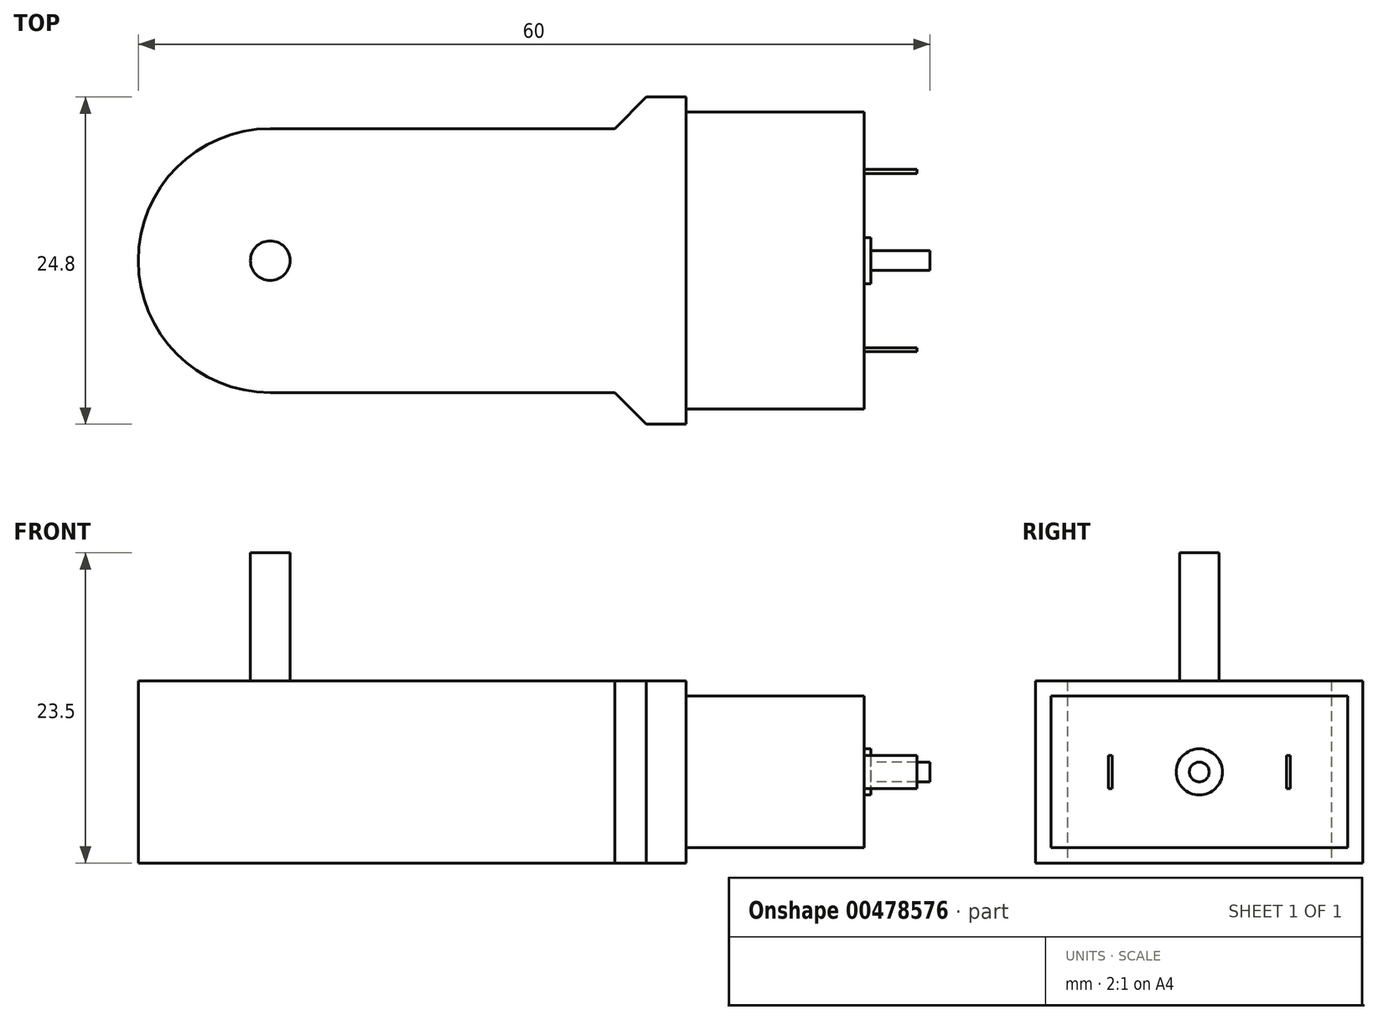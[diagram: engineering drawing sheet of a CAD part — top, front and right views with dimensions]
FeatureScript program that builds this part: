
annotation { "Feature Type Name" : "Feature", "Feature Type Description" : "" }
export const myFeature = defineFeature(function(context is Context, id is Id, definition is map)
    precondition{}
    {
        {
            var Q0;
            Q0=qCreatedBy(makeId("Top.planeOp"),FACE);
            var sketch = newSketch(context, id + "F0", { "sketchPlane" : qUnion([Q0])});
            skCircle(sketch, "E0", {"center": v(0, 0) * mm, "radius": 10 * mm});
            skLineSegment(sketch, "E1", {"start": v(0, 10) * mm, "end": v(26.1, 10) * mm});
            skLineSegment(sketch, "E2", {"start": v(26.1, 10) * mm, "end": v(28.5, 12.4) * mm});
            skLineSegment(sketch, "E3", {"start": v(28.5, 12.4) * mm, "end": v(31.5, 12.4) * mm});
            skLineSegment(sketch, "E4", {"start": v(31.5, 12.4) * mm, "end": v(31.5, 0) * mm});
            skLineSegment(sketch, "E5", {"start": v(0, 0) * mm, "end": v(31.5, 0) * mm, "construction": true});
            skLineSegment(sketch, "E6.MirrorCS", {"start": v(31.5, -12.4) * mm, "end": v(31.5, 0) * mm});
            skLineSegment(sketch, "E7.MirrorCS", {"start": v(28.5, -12.4) * mm, "end": v(31.5, -12.4) * mm});
            skLineSegment(sketch, "E8.MirrorCS", {"start": v(26.1, -10) * mm, "end": v(28.5, -12.4) * mm});
            skLineSegment(sketch, "E9.MirrorCS", {"start": v(0, -10) * mm, "end": v(26.1, -10) * mm});
            skSolve(sketch);
        }
        {
            var Q0;
            Q0 = qSketchRegion(id + "F0", true);
            extrude(context, id + "F1", {"entities" : qUnion([Q0]), "endBound" : BoundingType.SYMMETRIC, "depth" : 13.8 * mm});
        }
        {
            var Q0;
            Q0=qCreatedBy(makeId("Top.planeOp"),FACE);
            var sketch = newSketch(context, id + "F2", { "sketchPlane" : qUnion([Q0])});
            skCircle(sketch, "E10", {"center": v(0, 0) * mm, "radius": 1.5 * mm});
            skSolve(sketch);
        }
        {
            var Q0;
            Q0 = qSketchRegion(id + "F2", true);
            extrude(context, id + "F3", {"entities" : qUnion([Q0]), "operationType" : NewBodyOperationType.ADD, "depth" : 16.6 * mm});
        }
        {
            var Q0;
            Q0=qCreatedBy(makeId("Top.planeOp"),FACE);
            var sketch = newSketch(context, id + "F4", { "sketchPlane" : qUnion([Q0])});
            skPoint(sketch, "E11.0", {"position": v(31.5, 12.4) * mm});
            skPoint(sketch, "E12.0", {"position": v(31.5, -12.4) * mm});
            skLineSegment(sketch, "E13.bottom", {"start": v(31.5, -11.25) * mm, "end": v(45, -11.25) * mm});
            skLineSegment(sketch, "E13.top", {"start": v(31.5, 11.25) * mm, "end": v(45, 11.25) * mm});
            skLineSegment(sketch, "E13.left", {"start": v(31.5, -11.25) * mm, "end": v(31.5, 11.25) * mm});
            skLineSegment(sketch, "E13.right", {"start": v(45, -11.25) * mm, "end": v(45, 11.25) * mm});
            skLineSegment(sketch, "E14", {"start": v(31.5, 12.4) * mm, "end": v(31.5, 11.25) * mm, "construction": true});
            skLineSegment(sketch, "E15", {"start": v(0, 0) * mm, "end": v(31.5, 0) * mm, "construction": true});
            skSolve(sketch);
        }
        {
            var Q0;
            Q0=makeQuery(id+"F4.imprint","IMPRINT",FACE,{"disambiguationData":[TD([[makeQuery(id+"F4.imprint","IMPRINT",EDGE,{"derivedFrom":sQuery(id+"F4.wireOp",EDGE,"E13.bottom")}),1.0]])]});
            extrude(context, id + "F5", {"entities" : qUnion([Q0]), "operationType" : NewBodyOperationType.ADD, "endBound" : BoundingType.SYMMETRIC, "depth" : 11.5 * mm});
        }
        {
            var Q0;
            Q0=makeQuery(id+"F5.opExtrude","SWEPT_FACE",FACE,{"disambiguationData":[OSD([sQuery(id+"F4.wireOp",EDGE,"E13.right")])]});
            var sketch = newSketch(context, id + "F6", { "sketchPlane" : qUnion([Q0])});
            skLineSegment(sketch, "E16", {"start": v(-11.25, 0) * mm, "end": v(11.25, 0) * mm, "construction": true});
            skLineSegment(sketch, "E17", {"start": v(0, 5.75) * mm, "end": v(0, -5.75) * mm, "construction": true});
            skCircle(sketch, "E18", {"center": v(0, 0) * mm, "radius": 1.75 * mm});
            skSolve(sketch);
        }
        {
            var Q0;
            Q0 = qSketchRegion(id + "F6", true);
            extrude(context, id + "F7", {"entities" : qUnion([Q0]), "operationType" : NewBodyOperationType.ADD, "depth" : .5 * mm});
        }
        {
            var Q0;
            Q0=makeQuery(id+"F7.opExtrude","CAP_FACE",FACE,{"disambiguationData":[OSD([sQuery(id+"F6.wireOp",EDGE,"E18")])],"isStart":false});
            var sketch = newSketch(context, id + "F8", { "sketchPlane" : qUnion([Q0])});
            skCircle(sketch, "E19", {"center": v(0, 0) * mm, "radius": 0.75 * mm});
            skSolve(sketch);
        }
        {
            var Q0;
            Q0 = qSketchRegion(id + "F8", true);
            extrude(context, id + "F9", {"entities" : qUnion([Q0]), "operationType" : NewBodyOperationType.ADD, "depth" : 4.5 * mm});
        }
        {
            var Q0;
            Q0=makeQuery(id+"F5.opExtrude","SWEPT_FACE",FACE,{"disambiguationData":[OSD([sQuery(id+"F4.wireOp",EDGE,"E13.right")])]});
            var sketch = newSketch(context, id + "F10", { "sketchPlane" : qUnion([Q0])});
            skLineSegment(sketch, "E20", {"start": v(0, 5.75) * mm, "end": v(0, -5.75) * mm, "construction": true});
            skLineSegment(sketch, "E21.bottom", {"start": v(-6.9, 1.25) * mm, "end": v(-6.6, 1.25) * mm});
            skLineSegment(sketch, "E21.top", {"start": v(-6.9, -1.25) * mm, "end": v(-6.6, -1.25) * mm});
            skLineSegment(sketch, "E21.left", {"start": v(-6.9, 1.25) * mm, "end": v(-6.9, -1.25) * mm});
            skLineSegment(sketch, "E21.right", {"start": v(-6.6, 1.25) * mm, "end": v(-6.6, -1.25) * mm});
            skLineSegment(sketch, "E22", {"start": v(-6.6, 0) * mm, "end": v(0, 0) * mm, "construction": true});
            skLineSegment(sketch, "E23.MirrorCS", {"start": v(6.9, 1.25) * mm, "end": v(6.6, 1.25) * mm});
            skLineSegment(sketch, "E24.MirrorCS", {"start": v(6.9, -1.25) * mm, "end": v(6.6, -1.25) * mm});
            skLineSegment(sketch, "E25.MirrorCS", {"start": v(6.6, 1.25) * mm, "end": v(6.6, -1.25) * mm});
            skLineSegment(sketch, "E26.MirrorCS", {"start": v(6.9, 1.25) * mm, "end": v(6.9, -1.25) * mm});
            skLineSegment(sketch, "E27", {"start": v(-6.75, -1.25) * mm, "end": v(-6.75, 1.25) * mm, "construction": true});
            skLineSegment(sketch, "E28", {"start": v(6.75, -1.25) * mm, "end": v(6.75, 1.25) * mm, "construction": true});
            skSolve(sketch);
        }
        {
            var Q0;
            Q0 = qSketchRegion(id + "F10", true);
            extrude(context, id + "F11", {"entities" : qUnion([Q0]), "operationType" : NewBodyOperationType.ADD, "depth" : 4 * mm});
        }
    });
